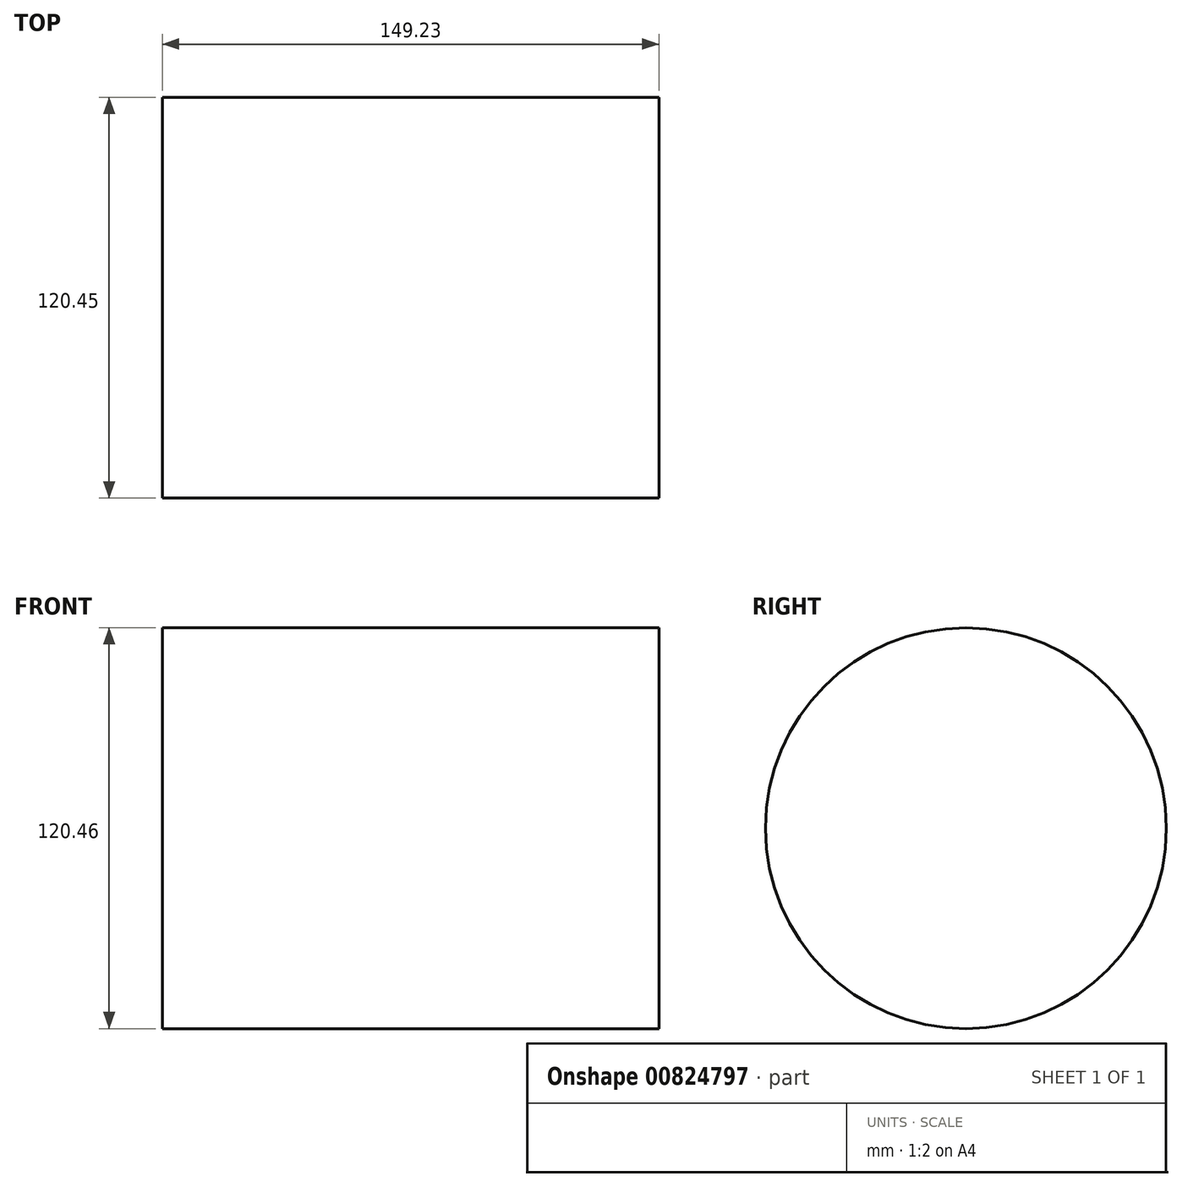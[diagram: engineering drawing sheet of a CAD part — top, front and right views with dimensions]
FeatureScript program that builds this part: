
annotation { "Feature Type Name" : "Feature", "Feature Type Description" : "" }
export const myFeature = defineFeature(function(context is Context, id is Id, definition is map)
    precondition{}
    {
        {
            var Q0;
            Q0=qCreatedBy(makeId("Top.planeOp"),FACE);
            var sketch = newSketch(context, id + "F0", { "sketchPlane" : qUnion([Q0])});
            skLineSegment(sketch, "E0.bottom", {"start": v(-74.14, 40.78) * mm, "end": v(75.09, 40.78) * mm});
            skLineSegment(sketch, "E0.top", {"start": v(-74.14, -19.55) * mm, "end": v(75.09, -19.55) * mm});
            skLineSegment(sketch, "E0.left", {"start": v(-74.14, 40.78) * mm, "end": v(-74.14, -19.55) * mm});
            skLineSegment(sketch, "E0.right", {"start": v(75.09, 40.78) * mm, "end": v(75.09, -19.55) * mm});
            skLineSegment(sketch, "E1", {"start": v(-74.14, -19.44) * mm, "end": v(75.56, -19.44) * mm});
            skSolve(sketch);
        }
        {
            var Q0;
            {var subQ0=sQuery(id+"F0.wireOp",EDGE,"E0.bottom");Q0=makeQuery(id+"F0.imprint","IMPRINT",FACE,{"disambiguationData":[TD([[makeQuery(id+"F0.imprint","IMPRINT",EDGE,{"derivedFrom":subQ0}),-1.0]])]});}
            var Q1;
            Q1=sQuery(id+"F0.wireOp",EDGE,"E1");
            revolve(context, id + "F1", {"surfaceOperationType" : NewSurfaceOperationType.NEW, "entities" : qUnion([Q0]), "axis" : qUnion([Q1]), "revolveType" : RevolveType.FULL});
        }
    });
